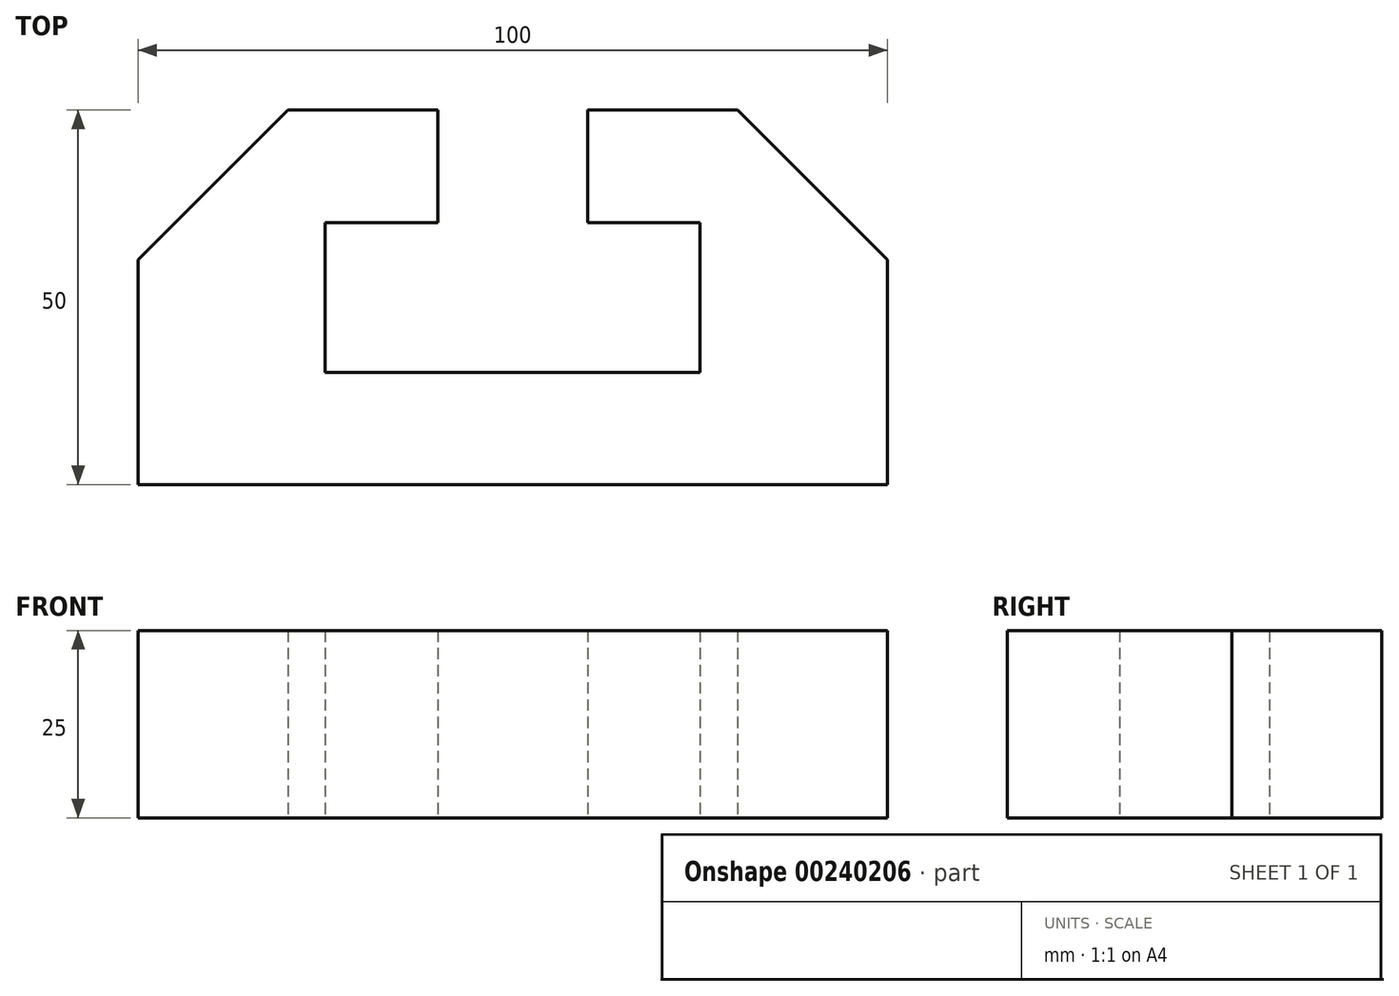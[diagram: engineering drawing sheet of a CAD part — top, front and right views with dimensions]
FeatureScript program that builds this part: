
annotation { "Feature Type Name" : "Feature", "Feature Type Description" : "" }
export const myFeature = defineFeature(function(context is Context, id is Id, definition is map)
    precondition{}
    {
        {
            var Q0;
            Q0=qCreatedBy(makeId("Top.planeOp"),FACE);
            var sketch = newSketch(context, id + "F0", { "sketchPlane" : qUnion([Q0])});
            skLineSegment(sketch, "E0", {"start": v(-25.02, 0) * mm, "end": v(24.98, 0) * mm});
            skLineSegment(sketch, "E1", {"start": v(24.98, 0) * mm, "end": v(24.98, 20) * mm});
            skLineSegment(sketch, "E2", {"start": v(24.98, 20) * mm, "end": v(9.98, 20) * mm});
            skLineSegment(sketch, "E3", {"start": v(9.98, 20) * mm, "end": v(9.98, 35) * mm});
            skLineSegment(sketch, "E4", {"start": v(-25.02, 0) * mm, "end": v(-25.02, 20) * mm});
            skLineSegment(sketch, "E5", {"start": v(-25.02, 20) * mm, "end": v(-10.02, 20) * mm});
            skLineSegment(sketch, "E6", {"start": v(-10.02, 20) * mm, "end": v(-10.02, 35) * mm});
            skLineSegment(sketch, "E7", {"start": v(9.98, 35) * mm, "end": v(29.98, 35) * mm});
            skLineSegment(sketch, "E8", {"start": v(-10.02, 35) * mm, "end": v(-30.02, 35) * mm});
            skLineSegment(sketch, "E9", {"start": v(50, -15) * mm, "end": v(0, -15) * mm});
            skLineSegment(sketch, "E10", {"start": v(0, -15) * mm, "end": v(-50, -15) * mm});
            skPoint(sketch, "E11.orphan", {"position": v(50, 35) * mm});
            skLineSegment(sketch, "E12", {"start": v(50, -15) * mm, "end": v(50, 15) * mm});
            skLineSegment(sketch, "E13", {"start": v(50, 15) * mm, "end": v(29.98, 35) * mm});
            skLineSegment(sketch, "E14", {"start": v(-50, -15) * mm, "end": v(-50, 15) * mm});
            skLineSegment(sketch, "E15", {"start": v(-30.02, 35) * mm, "end": v(-50, 15) * mm});
            skSolve(sketch);
        }
        {
            var Q0;
            Q0=makeQuery(id+"F0.imprint","IMPRINT",FACE,{"disambiguationData":[TD([[makeQuery(id+"F0.imprint","IMPRINT",EDGE,{"derivedFrom":sQuery(id+"F0.wireOp",EDGE,"E0")}),-1.0]])]});
            extrude(context, id + "F1", {"entities" : qUnion([Q0]), "depth" : 25 * mm});
        }
    });
